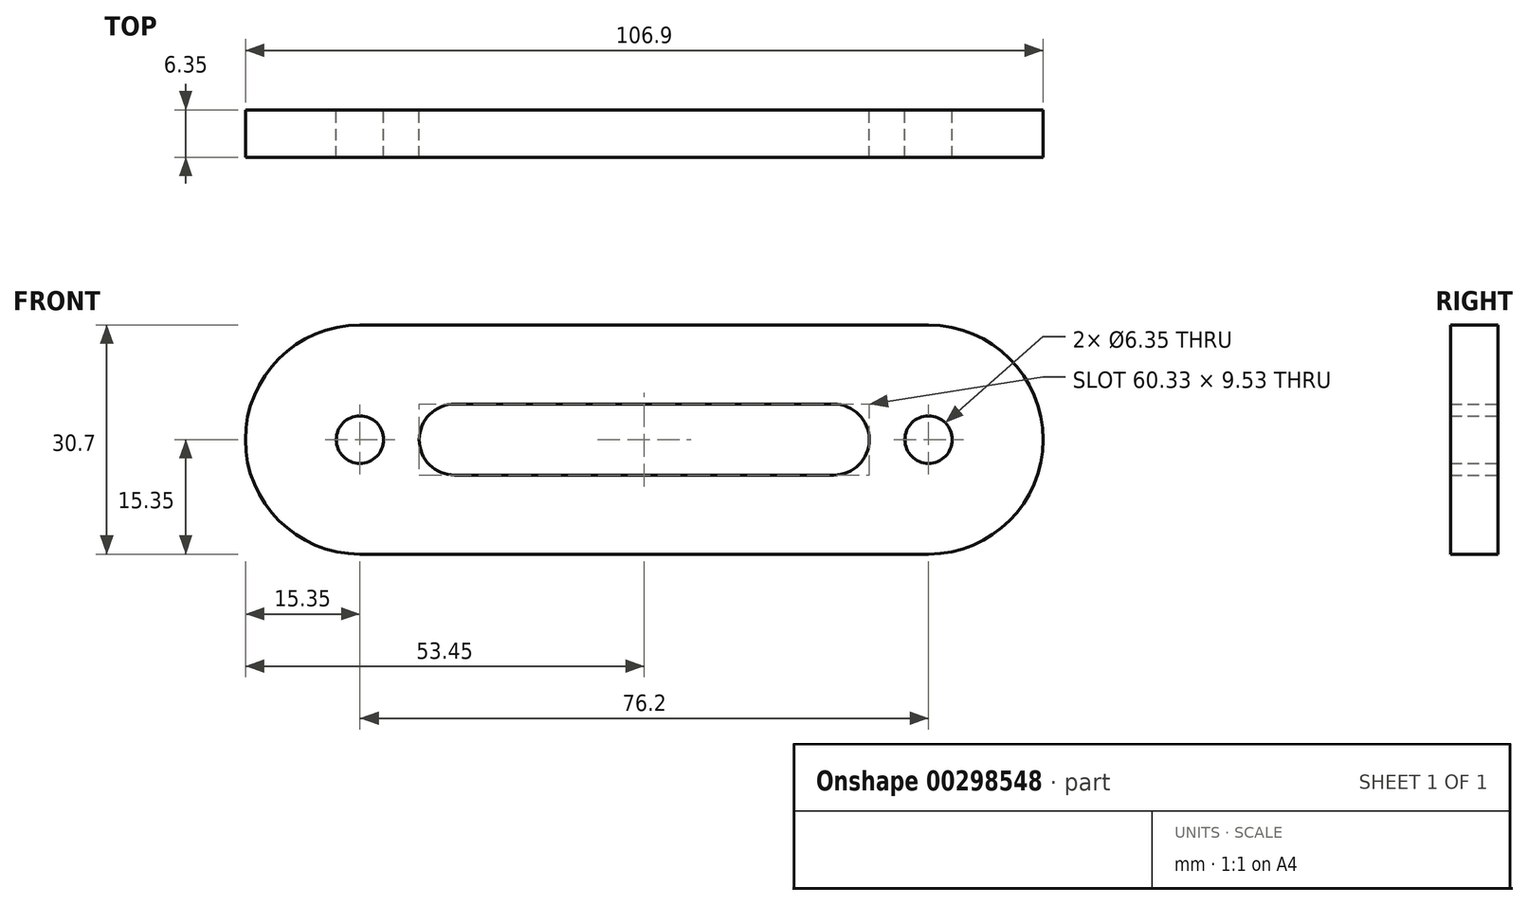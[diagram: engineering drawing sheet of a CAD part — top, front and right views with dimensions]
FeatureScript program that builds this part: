
annotation { "Feature Type Name" : "Feature", "Feature Type Description" : "" }
export const myFeature = defineFeature(function(context is Context, id is Id, definition is map)
    precondition{}
    {
        {
            var Q0;
            Q0=qCreatedBy(makeId("Front.planeOp"),FACE);
            var sketch = newSketch(context, id + "F0", { "sketchPlane" : qUnion([Q0])});
            skLineSegment(sketch, "E0.bottom", {"start": v(38.1, 15.35) * mm, "end": v(-38.1, 15.35) * mm});
            skLineSegment(sketch, "E0.top", {"start": v(38.1, -15.35) * mm, "end": v(-38.1, -15.35) * mm});
            skPoint(sketch, "E0.middle", {"position": v(0, 0) * mm});
            skArc(sketch, "E1", {"start": v(-38.1, 15.35) * mm, "mid": v(-53.45, 0) * mm, "end": v(-38.1, -15.35) * mm});
            skArc(sketch, "E2", {"start": v(38.1, -15.35) * mm, "mid": v(53.45, 0) * mm, "end": v(38.1, 15.35) * mm});
            skLineSegment(sketch, "E3.bottom", {"start": v(25.4, 4.76) * mm, "end": v(-25.4, 4.76) * mm});
            skLineSegment(sketch, "E3.top", {"start": v(25.4, -4.76) * mm, "end": v(-25.4, -4.76) * mm});
            skCircle(sketch, "E4", {"center": v(-38.1, 0) * mm, "radius": 3.18 * mm});
            skCircle(sketch, "E5", {"center": v(38.1, 0) * mm, "radius": 3.18 * mm});
            skArc(sketch, "E6", {"start": v(-25.4, 4.76) * mm, "mid": v(-30.16, 0) * mm, "end": v(-25.4, -4.76) * mm});
            skArc(sketch, "E7", {"start": v(25.4, -4.76) * mm, "mid": v(30.16, 0) * mm, "end": v(25.4, 4.76) * mm});
            skSolve(sketch);
        }
        {
            var Q0;
            Q0=qSketchRegion(id+"F0",true);
            var Q1;
            Q1=makeQuery(id+"F0.imprint","IMPRINT",FACE,{"disambiguationData":[TD([[makeQuery(id+"F0.imprint","IMPRINT",EDGE,{"derivedFrom":sQuery(id+"F0.wireOp",EDGE,"E0.bottom")}),1.0]])]});
            extrude(context, id + "F1", {"entities" : qUnion([Q0, Q1]), "depth" : 6.35 * mm});
        }
    });
